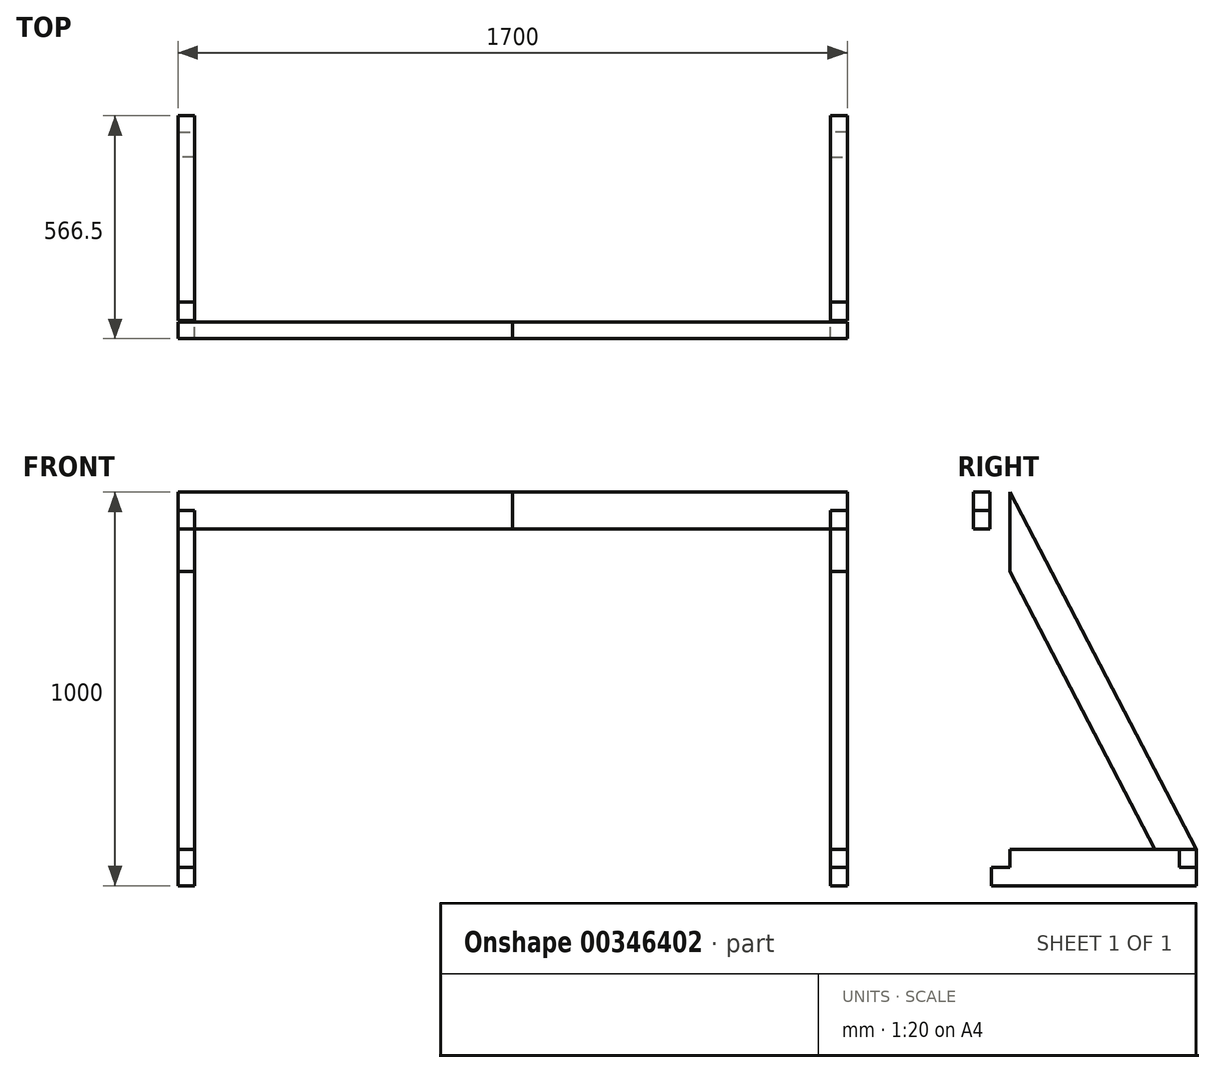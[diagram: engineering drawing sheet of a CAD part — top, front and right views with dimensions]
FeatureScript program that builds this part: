
annotation { "Feature Type Name" : "Feature", "Feature Type Description" : "" }
export const myFeature = defineFeature(function(context is Context, id is Id, definition is map)
    precondition{}
    {
        {
            var Q0;
            Q0=qCreatedBy(makeId("Front.planeOp"),FACE);
            var sketch = newSketch(context, id + "F0", { "sketchPlane" : qUnion([Q0])});
            skLineSegment(sketch, "E0.bottom", {"start": v(0, 1000) * mm, "end": v(-808, 1000) * mm});
            skLineSegment(sketch, "E0.top", {"start": v(0, 1093) * mm, "end": v(-850, 1093) * mm});
            skLineSegment(sketch, "E0.left", {"start": v(0, 1000) * mm, "end": v(0, 1093) * mm});
            skLineSegment(sketch, "E0.right", {"start": v(-850, 1046.5) * mm, "end": v(-850, 1093) * mm});
            skLineSegment(sketch, "E1", {"start": v(-850, 1046.5) * mm, "end": v(-808, 1046.5) * mm});
            skLineSegment(sketch, "E2", {"start": v(-808, 1046.5) * mm, "end": v(-808, 1000) * mm});
            skPoint(sketch, "E3.orphan", {"position": v(-850, 1000) * mm});
            skSolve(sketch);
        }
        {
            var Q0;
            Q0=qSketchRegion(id+"F0",true);
            extrude(context, id + "F1", {"entities" : qUnion([Q0]), "depth" : 42 * mm});
        }
        {
            var Q0;
            Q0=makeQuery(id+"F1.opExtrude","SWEPT_FACE",FACE,{"disambiguationData":[OSD([sQuery(id+"F0.wireOp",EDGE,"E2")])]});
            var sketch = newSketch(context, id + "F2", { "sketchPlane" : qUnion([Q0])});
            skLineSegment(sketch, "E4.0", {"start": v(0, 1046.5) * mm, "end": v(0, 1093) * mm});
            skLineSegment(sketch, "E5.0", {"start": v(42, 1046.5) * mm, "end": v(0, 1046.5) * mm});
            skLineSegment(sketch, "E6.0", {"start": v(42, 1046.5) * mm, "end": v(42, 1000) * mm});
            skLineSegment(sketch, "E7", {"start": v(0, 1093) * mm, "end": v(0, 1046.5) * mm});
            skLineSegment(sketch, "E8", {"start": v(42, 1046.5) * mm, "end": v(42, 93) * mm});
            skLineSegment(sketch, "E9", {"start": v(42, 93) * mm, "end": v(-4.5, 93) * mm});
            skLineSegment(sketch, "E10", {"start": v(-4.5, 93) * mm, "end": v(-4.5, 139.5) * mm});
            skLineSegment(sketch, "E11", {"start": v(-4.5, 139.5) * mm, "end": v(-51, 139.5) * mm});
            skLineSegment(sketch, "E12", {"start": v(-51, 139.5) * mm, "end": v(-51, 1093) * mm});
            skLineSegment(sketch, "E13", {"start": v(-51, 1093) * mm, "end": v(0, 1093) * mm});
            skSolve(sketch);
        }
        {
            var Q0;
            Q0=makeQuery(id+"F2.imprint","IMPRINT",FACE,{"disambiguationData":[TD([[makeQuery(id+"F2.imprint","IMPRINT",EDGE,{"derivedFrom":sQuery(id+"F2.wireOp",EDGE,"E7")}),-1.0]])]});
            var Q1;
            {var subQ3=sQuery(id+"F2.wireOp",EDGE,"E5.0");Q1=makeQuery(id+"F2.imprint","IMPRINT",FACE,{"disambiguationData":[TD([[makeQuery(id+"F2.imprint","IMPRINT",EDGE,{"derivedFrom":subQ3}),1.0]])]});}
            var Q2;
            Q2=makeQuery(id+"F1.opExtrude","SWEPT_FACE",FACE,{"disambiguationData":[OSD([sQuery(id+"F0.wireOp",EDGE,"E0.right")])]});
            extrude(context, id + "F3", {"entities" : qUnion([Q0, Q1]), "endBound" : BoundingType.UP_TO_SURFACE, "endBoundEntityFace" : qUnion([Q2]), "depth" : 25 * mm});
        }
        {
            var Q0;
            Q0=makeQuery(id+"F3.opExtrude","CAP_FACE",FACE,{"disambiguationData":[OSD([sQuery(id+"F2.wireOp",EDGE,"E5.0"),sQuery(id+"F2.wireOp",EDGE,"E7"),sQuery(id+"F2.wireOp",EDGE,"E8"),sQuery(id+"F2.wireOp",EDGE,"E9"),sQuery(id+"F2.wireOp",EDGE,"E10"),sQuery(id+"F2.wireOp",EDGE,"E11"),sQuery(id+"F2.wireOp",EDGE,"E12"),sQuery(id+"F2.wireOp",EDGE,"E13")])],"isStart":true});
            var sketch = newSketch(context, id + "F4", { "sketchPlane" : qUnion([Q0])});
            skLineSegment(sketch, "E14", {"start": v(51, 139.5) * mm, "end": v(4.5, 139.5) * mm});
            skLineSegment(sketch, "E15", {"start": v(4.5, 139.5) * mm, "end": v(4.5, 93) * mm});
            skLineSegment(sketch, "E16", {"start": v(4.5, 93) * mm, "end": v(524.5, 93) * mm});
            skLineSegment(sketch, "E17", {"start": v(524.5, 93) * mm, "end": v(524.5, 139.5) * mm});
            skLineSegment(sketch, "E18", {"start": v(524.5, 139.5) * mm, "end": v(482.5, 139.5) * mm});
            skLineSegment(sketch, "E19", {"start": v(482.5, 139.5) * mm, "end": v(482.5, 186) * mm});
            skLineSegment(sketch, "E20", {"start": v(482.5, 186) * mm, "end": v(51, 186) * mm});
            skLineSegment(sketch, "E21", {"start": v(51, 186) * mm, "end": v(51, 139.5) * mm});
            skSolve(sketch);
        }
        {
            var Q0;
            Q0=qSketchRegion(id+"F4",true);
            var Q1;
            Q1=makeQuery(id+"F3.opExtrude","CAP_FACE",FACE,{"disambiguationData":[OSD([sQuery(id+"F2.wireOp",EDGE,"E5.0"),sQuery(id+"F2.wireOp",EDGE,"E7"),sQuery(id+"F2.wireOp",EDGE,"E8"),sQuery(id+"F2.wireOp",EDGE,"E9"),sQuery(id+"F2.wireOp",EDGE,"E10"),sQuery(id+"F2.wireOp",EDGE,"E11"),sQuery(id+"F2.wireOp",EDGE,"E12"),sQuery(id+"F2.wireOp",EDGE,"E13")])],"isStart":false});
            extrude(context, id + "F5", {"entities" : qUnion([Q0]), "endBound" : BoundingType.UP_TO_SURFACE, "oppositeDirection" : true, "endBoundEntityFace" : qUnion([Q1]), "depth" : 25 * mm});
        }
        {
            var Q0;
            Q0=makeQuery(id+"F3.opExtrude","CAP_FACE",FACE,{"disambiguationData":[OSD([sQuery(id+"F2.wireOp",EDGE,"E5.0"),sQuery(id+"F2.wireOp",EDGE,"E7"),sQuery(id+"F2.wireOp",EDGE,"E8"),sQuery(id+"F2.wireOp",EDGE,"E9"),sQuery(id+"F2.wireOp",EDGE,"E10"),sQuery(id+"F2.wireOp",EDGE,"E11"),sQuery(id+"F2.wireOp",EDGE,"E12"),sQuery(id+"F2.wireOp",EDGE,"E13")])],"isStart":false});
            var sketch = newSketch(context, id + "F6", { "sketchPlane" : qUnion([Q0])});
            skLineSegment(sketch, "E22.0", {"start": v(-482.5, 186) * mm, "end": v(-51, 186) * mm});
            skLineSegment(sketch, "E23.0", {"start": v(-524.5, 93) * mm, "end": v(-524.5, 139.5) * mm});
            skLineSegment(sketch, "E24.0", {"start": v(-51, 139.5) * mm, "end": v(-51, 1093) * mm});
            skLineSegment(sketch, "E25.0", {"start": v(-51, 1093) * mm, "end": v(0, 1093) * mm});
            skLineSegment(sketch, "E26", {"start": v(-482.5, 186) * mm, "end": v(-635.91, 186) * mm, "construction": true});
            skLineSegment(sketch, "E27", {"start": v(-524.5, 93) * mm, "end": v(-524.5, 301.2) * mm, "construction": true});
            skLineSegment(sketch, "E28", {"start": v(-51, 1093) * mm, "end": v(-524.5, 186) * mm});
            skLineSegment(sketch, "E29", {"start": v(-419.59, 186) * mm, "end": v(-51, 892.04) * mm});
            skLineSegment(sketch, "E30", {"start": v(-51, 892.04) * mm, "end": v(-51, 1093) * mm});
            skLineSegment(sketch, "E31", {"start": v(-524.5, 186) * mm, "end": v(-419.59, 186) * mm});
            skSolve(sketch);
        }
        {
            var Q0;
            {var subQ1=sQuery(id+"F6.wireOp",EDGE,"E28");Q0=makeQuery(id+"F6.imprint","IMPRINT",FACE,{"disambiguationData":[TD([[makeQuery(id+"F6.imprint","IMPRINT",EDGE,{"derivedFrom":subQ1}),1.0]])]});}
            var Q1;
            Q1=makeQuery(id+"F5.opExtrude","CAP_FACE",FACE,{"disambiguationData":[OSD([sQuery(id+"F4.wireOp",EDGE,"E14"),sQuery(id+"F4.wireOp",EDGE,"E15"),sQuery(id+"F4.wireOp",EDGE,"E16"),sQuery(id+"F4.wireOp",EDGE,"E17"),sQuery(id+"F4.wireOp",EDGE,"E18"),sQuery(id+"F4.wireOp",EDGE,"E19"),sQuery(id+"F4.wireOp",EDGE,"E20"),sQuery(id+"F4.wireOp",EDGE,"E21")])],"isStart":true});
            extrude(context, id + "F7", {"entities" : qUnion([Q0]), "endBound" : BoundingType.UP_TO_SURFACE, "oppositeDirection" : true, "endBoundEntityFace" : qUnion([Q1]), "depth" : 25 * mm});
        }
        {
            var Q0;
            Q0=makeQuery(id+"F5.opExtrude","SWEPT_FACE",FACE,{"disambiguationData":[OSD([sQuery(id+"F4.wireOp",EDGE,"E19")])]});
            var sketch = newSketch(context, id + "F8", { "sketchPlane" : qUnion([Q0])});
            skLineSegment(sketch, "E32", {"start": v(850, 186) * mm, "end": v(850, 139.5) * mm});
            skLineSegment(sketch, "E33", {"start": v(850, 139.5) * mm, "end": v(808, 139.5) * mm});
            skLineSegment(sketch, "E34.0", {"start": v(808, 93) * mm, "end": v(808, 139.5) * mm});
            skLineSegment(sketch, "E35", {"start": v(808, 139.5) * mm, "end": v(808, 93) * mm});
            skLineSegment(sketch, "E36", {"start": v(808, 93) * mm, "end": v(0, 93) * mm});
            skLineSegment(sketch, "E37", {"start": v(0, 93) * mm, "end": v(0, 186) * mm});
            skLineSegment(sketch, "E38", {"start": v(0, 186) * mm, "end": v(850, 186) * mm});
            skSolve(sketch);
        }
        {
            var Q0;
            Q0=makeQuery(id+"F8.imprint","IMPRINT",FACE,{"disambiguationData":[TD([[makeQuery(id+"F8.imprint","IMPRINT",EDGE,{"derivedFrom":sQuery(id+"F8.wireOp",EDGE,"E35")}),-1.0]])]});
            var Q1;
            {var subQ2=sQuery(id+"F8.wireOp",EDGE,"E32");Q1=makeQuery(id+"F8.imprint","IMPRINT",FACE,{"disambiguationData":[TD([[makeQuery(id+"F8.imprint","IMPRINT",EDGE,{"derivedFrom":subQ2}),1.0]])]});}
            var Q2;
            Q2=makeQuery(id+"F5.opExtrude","SWEPT_FACE",FACE,{"disambiguationData":[OSD([sQuery(id+"F4.wireOp",EDGE,"E17")])]});
            extrude(context, id + "F9", {"entities" : qUnion([Q0, Q1]), "endBound" : BoundingType.UP_TO_SURFACE, "endBoundEntityFace" : qUnion([Q2]), "depth" : 25 * mm});
        }
        {
            var Q0;
            Q0=makeQuery(id+"F1.opExtrude","SWEPT_BODY",BODY,{"disambiguationData":[OSD([sQuery(id+"F0.wireOp",EDGE,"E0.bottom"),sQuery(id+"F0.wireOp",EDGE,"E0.top"),sQuery(id+"F0.wireOp",EDGE,"E0.left"),sQuery(id+"F0.wireOp",EDGE,"E0.right"),sQuery(id+"F0.wireOp",EDGE,"E1"),sQuery(id+"F0.wireOp",EDGE,"E2")])]});
            var Q1;
            Q1=makeQuery(id+"F7.opExtrude","SWEPT_BODY",BODY,{"disambiguationData":[OSD([sQuery(id+"F6.wireOp",EDGE,"E28"),sQuery(id+"F6.wireOp",EDGE,"E29"),sQuery(id+"F6.wireOp",EDGE,"E30"),sQuery(id+"F6.wireOp",EDGE,"E31")])]});
            var Q2;
            Q2=makeQuery(id+"F3.opExtrude","SWEPT_BODY",BODY,{"disambiguationData":[OSD([sQuery(id+"F2.wireOp",EDGE,"E5.0"),sQuery(id+"F2.wireOp",EDGE,"E7"),sQuery(id+"F2.wireOp",EDGE,"E8"),sQuery(id+"F2.wireOp",EDGE,"E9"),sQuery(id+"F2.wireOp",EDGE,"E10"),sQuery(id+"F2.wireOp",EDGE,"E11"),sQuery(id+"F2.wireOp",EDGE,"E12"),sQuery(id+"F2.wireOp",EDGE,"E13")])]});
            var Q3;
            Q3=makeQuery(id+"F5.opExtrude","SWEPT_BODY",BODY,{"disambiguationData":[OSD([sQuery(id+"F4.wireOp",EDGE,"E14"),sQuery(id+"F4.wireOp",EDGE,"E15"),sQuery(id+"F4.wireOp",EDGE,"E16"),sQuery(id+"F4.wireOp",EDGE,"E17"),sQuery(id+"F4.wireOp",EDGE,"E18"),sQuery(id+"F4.wireOp",EDGE,"E19"),sQuery(id+"F4.wireOp",EDGE,"E20"),sQuery(id+"F4.wireOp",EDGE,"E21")])]});
            var Q4;
            Q4=makeQuery(id+"F9.opExtrude","SWEPT_BODY",BODY,{"disambiguationData":[OSD([sQuery(id+"F8.wireOp",EDGE,"E32"),sQuery(id+"F8.wireOp",EDGE,"E33"),sQuery(id+"F8.wireOp",EDGE,"E35"),sQuery(id+"F8.wireOp",EDGE,"E36"),sQuery(id+"F8.wireOp",EDGE,"E37"),sQuery(id+"F8.wireOp",EDGE,"E38")])]});
            var Q5;
            Q5=makeQuery(id+"F1.opExtrude","SWEPT_FACE",FACE,{"disambiguationData":[OSD([sQuery(id+"F0.wireOp",EDGE,"E0.left")])]});
            mirror(context, id + "F10", {"entities" : qUnion([Q0, Q1, Q2, Q3, Q4]), "mirrorPlane" : qUnion([Q5])});
        }
    });
